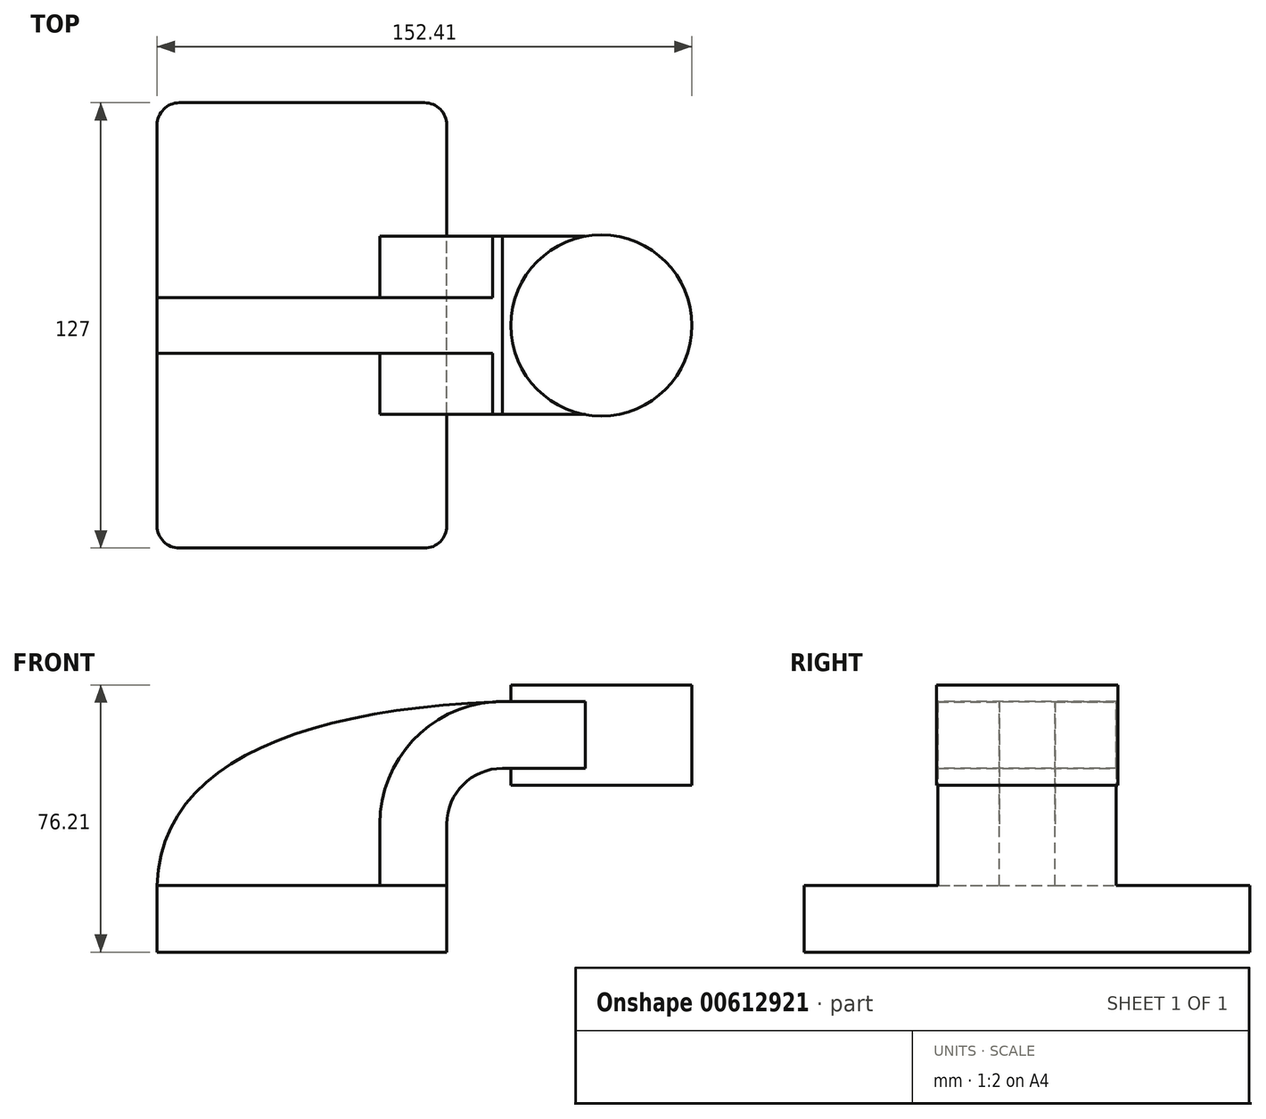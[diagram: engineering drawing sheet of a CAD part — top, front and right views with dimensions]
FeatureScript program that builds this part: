
annotation { "Feature Type Name" : "Feature", "Feature Type Description" : "" }
export const myFeature = defineFeature(function(context is Context, id is Id, definition is map)
    precondition{}
    {
        {
            var Q0;
            Q0=qCreatedBy(makeId("Front.planeOp"),FACE);
            var sketch = newSketch(context, id + "F0", { "sketchPlane" : qUnion([Q0])});
            skLineSegment(sketch, "E0.bottom", {"start": v(-41.28, -9.53) * mm, "end": v(41.28, -9.53) * mm});
            skLineSegment(sketch, "E0.top", {"start": v(-41.28, 9.52) * mm, "end": v(41.28, 9.52) * mm});
            skLineSegment(sketch, "E0.left", {"start": v(-41.28, -9.53) * mm, "end": v(-41.28, 9.53) * mm});
            skLineSegment(sketch, "E0.right", {"start": v(41.28, -9.53) * mm, "end": v(41.28, 9.52) * mm});
            skPoint(sketch, "E0.middle", {"position": v(0, 0) * mm});
            skLineSegment(sketch, "E1", {"start": v(41.27, 9.52) * mm, "end": v(41.27, 27) * mm});
            skLineSegment(sketch, "E2.bottom", {"start": v(111.12, 38.1) * mm, "end": v(60.32, 38.1) * mm});
            skLineSegment(sketch, "E2.top", {"start": v(111.12, 66.68) * mm, "end": v(60.32, 66.68) * mm});
            skLineSegment(sketch, "E2.left", {"start": v(111.12, 38.1) * mm, "end": v(111.12, 66.68) * mm});
            skLineSegment(sketch, "E2.right", {"start": v(60.32, 38.1) * mm, "end": v(60.32, 66.68) * mm});
            skPoint(sketch, "E2.middle", {"position": v(85.72, 52.39) * mm});
            skArc(sketch, "E3", {"start": v(41.27, 27) * mm, "mid": v(45.92, 38.23) * mm, "end": v(57.15, 42.88) * mm});
            skLineSegment(sketch, "E4", {"start": v(57.15, 42.88) * mm, "end": v(85.3, 42.88) * mm});
            skLineSegment(sketch, "E5.0", {"start": v(57.15, 61.93) * mm, "end": v(85.3, 61.93) * mm});
            skArc(sketch, "E5.1", {"start": v(22.22, 27) * mm, "mid": v(32.45, 51.7) * mm, "end": v(57.15, 61.93) * mm});
            skLineSegment(sketch, "E5.2", {"start": v(22.22, 9.52) * mm, "end": v(22.22, 27) * mm});
            skLineSegment(sketch, "E6", {"start": v(85.3, 66.68) * mm, "end": v(85.3, 38.1) * mm});
            skFitSpline(sketch, "E7", {"points": [v(-41.28, 9.53) * mm, v(57.15, 61.93) * mm], "startDerivative": vector(3.03, 105) * mm, "endDerivative": vector(171.45, 6.21) * mm});
            skSolve(sketch);
        }
        {
            var Q0;
            Q0=makeQuery(id+"F0.imprint","IMPRINT",FACE,{"disambiguationData":[TD([[makeQuery(id+"F0.imprint","IMPRINT",EDGE,{"derivedFrom":sQuery(id+"F0.wireOp",EDGE,"E0.bottom")}),1.0]])]});
            extrude(context, id + "F1", {"entities" : qUnion([Q0]), "endBound" : BoundingType.SYMMETRIC, "depth" : 127 * mm, "offsetDistance" : 25.4 * mm});
        }
        {
            var Q0;
            {var subQ1=sQuery(id+"F0.wireOp",EDGE,"E1");Q0=makeQuery(id+"F0.imprint","IMPRINT",FACE,{"disambiguationData":[TD([[makeQuery(id+"F0.imprint","IMPRINT",EDGE,{"derivedFrom":subQ1}),1.0]])]});}
            var Q1;
            {var subQ0=sQuery(id+"F0.wireOp",EDGE,"E4");var subQ1=sQuery(id+"F0.wireOp",EDGE,"E2.right");var subQ2=makeQuery(id+"F0.imprint","INTERSECT",VERTEX,{"derivedFrom":[subQ1,subQ0]});Q1=makeQuery(id+"F0.imprint","IMPRINT",FACE,{"disambiguationData":[TD([[makeQuery(id+"F0.imprint","IMPRINT",EDGE,{"disambiguationData":[TD([[subQ2,-1.0]])],"derivedFrom":subQ1}),-1.0]])]});}
            extrude(context, id + "F2", {"entities" : qUnion([Q0, Q1]), "operationType" : NewBodyOperationType.ADD, "endBound" : BoundingType.SYMMETRIC, "depth" : 50.8 * mm, "offsetDistance" : 25.4 * mm});
        }
        {
            var Q0;
            {var subQ3=sQuery(id+"F0.wireOp",EDGE,"E5.2");Q0=makeQuery(id+"F0.imprint","IMPRINT",FACE,{"disambiguationData":[TD([[makeQuery(id+"F0.imprint","IMPRINT",EDGE,{"derivedFrom":subQ3}),1.0]])]});}
            extrude(context, id + "F3", {"entities" : qUnion([Q0]), "operationType" : NewBodyOperationType.ADD, "endBound" : BoundingType.SYMMETRIC, "depth" : 15.88 * mm, "offsetDistance" : 25.4 * mm});
        }
        {
            var Q0;
            {var subQ4=sQuery(id+"F0.wireOp",EDGE,"E2.left");Q0=makeQuery(id+"F0.imprint","IMPRINT",FACE,{"disambiguationData":[TD([[makeQuery(id+"F0.imprint","IMPRINT",EDGE,{"derivedFrom":subQ4}),1.0]])]});}
            var Q1;
            Q1=sQuery(id+"F0.wireOp",EDGE,"E6");
            revolve(context, id + "F4", {"operationType" : NewBodyOperationType.ADD, "entities" : qUnion([Q0]), "axis" : qUnion([Q1]), "revolveType" : RevolveType.FULL});
        }
        {
            var Q0;
            Q0=makeQuery(id+"F1.opExtrude","CAP_EDGE",EDGE,{"disambiguationData":[OSD([sQuery(id+"F0.wireOp",EDGE,"E0.left")])],"isStart":false});
            var Q1;
            Q1=makeQuery(id+"F1.opExtrude","CAP_EDGE",EDGE,{"disambiguationData":[OSD([sQuery(id+"F0.wireOp",EDGE,"E0.right")])],"isStart":false});
            var Q2;
            Q2=makeQuery(id+"F1.opExtrude","CAP_EDGE",EDGE,{"disambiguationData":[OSD([sQuery(id+"F0.wireOp",EDGE,"E0.right")])],"isStart":true});
            var Q3;
            Q3=makeQuery(id+"F1.opExtrude","CAP_EDGE",EDGE,{"disambiguationData":[OSD([sQuery(id+"F0.wireOp",EDGE,"E0.left")])],"isStart":true});
            fillet(context, id + "F5", {"entities" : qUnion([Q0, Q1, Q2, Q3]), "radius" : 6.35 * mm, "tangentPropagation" : true, "allowEdgeOverflow" : false});
        }
    });
